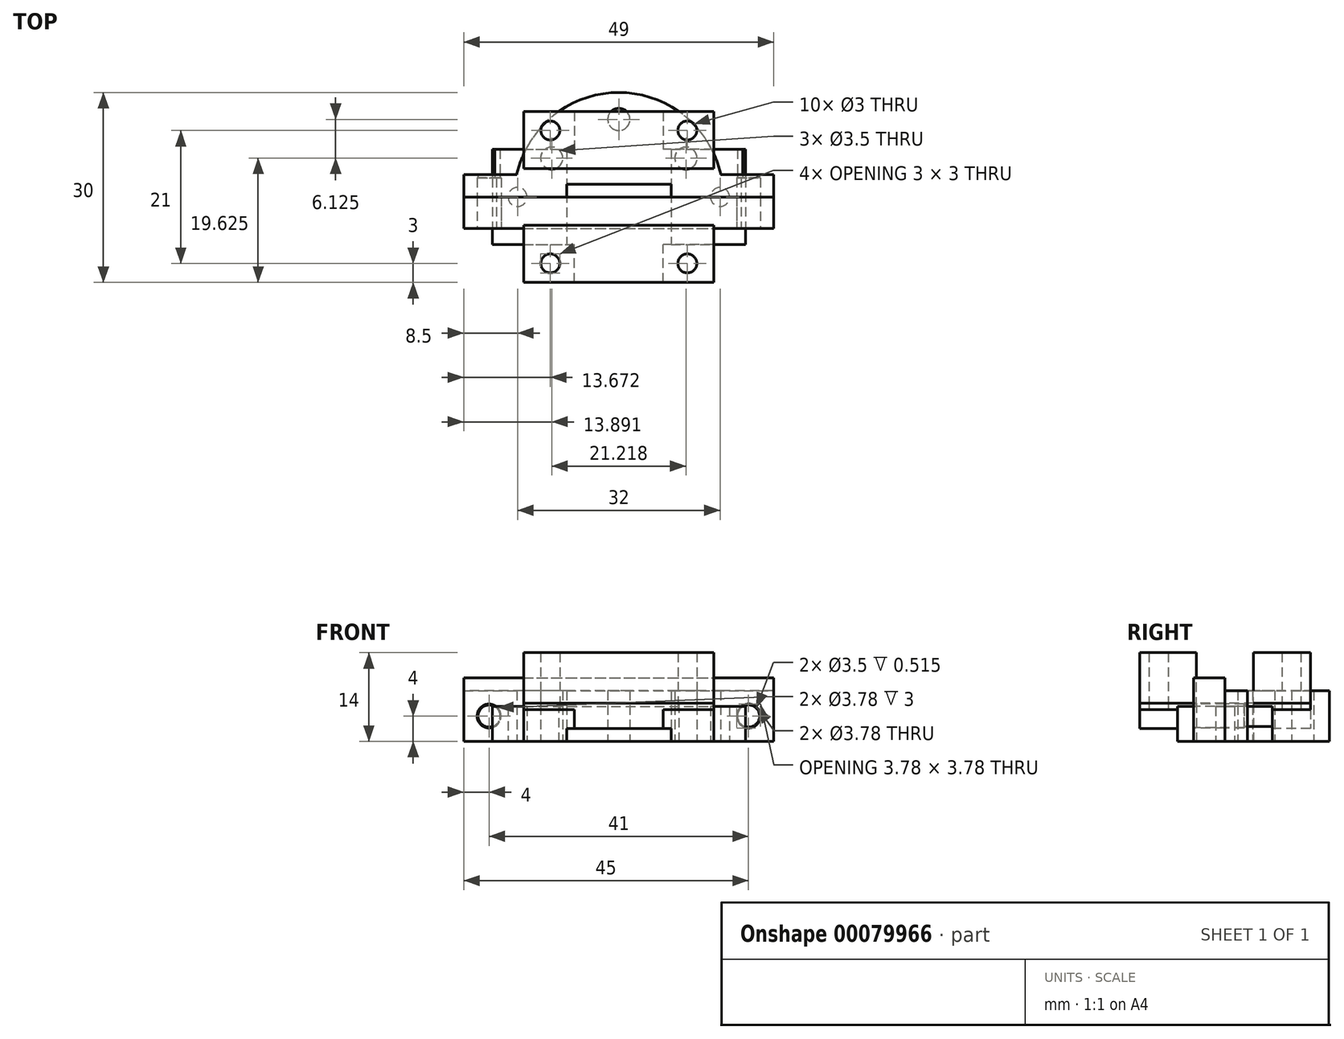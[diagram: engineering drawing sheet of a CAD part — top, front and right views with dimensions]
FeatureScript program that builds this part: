
annotation { "Feature Type Name" : "Feature", "Feature Type Description" : "" }
export const myFeature = defineFeature(function(context is Context, id is Id, definition is map)
    precondition{}
    {
        {
            var Q0;
            Q0=qCreatedBy(makeId("Top.planeOp"),FACE);
            var sketch = newSketch(context, id + "F0", { "sketchPlane" : qUnion([Q0])});
            skLineSegment(sketch, "E0.bottom", {"start": v(-20, 7.5) * mm, "end": v(20, 7.5) * mm});
            skLineSegment(sketch, "E0.top", {"start": v(-20, -7.5) * mm, "end": v(20, -7.5) * mm});
            skLineSegment(sketch, "E0.left", {"start": v(-20, 7.5) * mm, "end": v(-20, -7.5) * mm});
            skLineSegment(sketch, "E0.right", {"start": v(20, 7.5) * mm, "end": v(20, -7.5) * mm});
            skPoint(sketch, "E1", {"position": v(0, 7.5) * mm});
            skPoint(sketch, "E2", {"position": v(20, 0) * mm});
            skLineSegment(sketch, "E3.bottom", {"start": v(-15, 13.5) * mm, "end": v(15, 13.5) * mm});
            skLineSegment(sketch, "E3.top", {"start": v(-15, 7.5) * mm, "end": v(15, 7.5) * mm});
            skLineSegment(sketch, "E3.left", {"start": v(-15, 13.5) * mm, "end": v(-15, 7.5) * mm});
            skLineSegment(sketch, "E3.right", {"start": v(15, 13.5) * mm, "end": v(15, 7.5) * mm});
            skPoint(sketch, "E4", {"position": v(0, 13.5) * mm});
            skLineSegment(sketch, "E5.bottom", {"start": v(-15, -7.5) * mm, "end": v(15, -7.5) * mm});
            skLineSegment(sketch, "E5.top", {"start": v(-15, -13.5) * mm, "end": v(15, -13.5) * mm});
            skLineSegment(sketch, "E5.left", {"start": v(-15, -7.5) * mm, "end": v(-15, -13.5) * mm});
            skLineSegment(sketch, "E5.right", {"start": v(15, -7.5) * mm, "end": v(15, -13.5) * mm});
            skPoint(sketch, "E6", {"position": v(0, -13.5) * mm});
            skCircle(sketch, "E7", {"center": v(-10.83, 10.5) * mm, "radius": 1.5 * mm});
            skPoint(sketch, "E8", {"position": v(-15, 10.5) * mm});
            skCircle(sketch, "E9.MirrorC", {"center": v(10.83, 10.5) * mm, "radius": 1.5 * mm});
            skCircle(sketch, "E10.MirrorC", {"center": v(-10.83, -10.5) * mm, "radius": 1.5 * mm});
            skCircle(sketch, "E11.MirrorC", {"center": v(10.83, -10.5) * mm, "radius": 1.5 * mm});
            skCircle(sketch, "E12", {"center": v(-16, 0) * mm, "radius": 1.5 * mm});
            skCircle(sketch, "E13.MirrorC", {"center": v(16, 0) * mm, "radius": 1.5 * mm});
            skSolve(sketch);
        }
        {
            var Q0;
            Q0 = qSketchRegion(id + "F0", true);
            extrude(context, id + "F1", {"entities" : qUnion([Q0]), "depth" : 14 * mm});
        }
        {
            var Q0;
            Q0=makeQuery(id+"F1.opExtrude","CAP_FACE",FACE,{"disambiguationData":[OSD([sQuery(id+"F0.wireOp",EDGE,"E0.left"),sQuery(id+"F0.wireOp",EDGE,"E0.right"),sQuery(id+"F0.wireOp",EDGE,"E3.bottom"),sQuery(id+"F0.wireOp",EDGE,"E3.top"),sQuery(id+"F0.wireOp",EDGE,"E3.left"),sQuery(id+"F0.wireOp",EDGE,"E3.right"),sQuery(id+"F0.wireOp",EDGE,"E5.bottom"),sQuery(id+"F0.wireOp",EDGE,"E5.top"),sQuery(id+"F0.wireOp",EDGE,"E5.left"),sQuery(id+"F0.wireOp",EDGE,"E5.right")])],"isStart":false});
            var sketch = newSketch(context, id + "F2", { "sketchPlane" : qUnion([Q0])});
            skLineSegment(sketch, "E14.bottom", {"start": v(-15, 4.5) * mm, "end": v(15, 4.5) * mm});
            skLineSegment(sketch, "E14.top", {"start": v(-15, -4.5) * mm, "end": v(15, -4.5) * mm});
            skLineSegment(sketch, "E14.left", {"start": v(-20, 4.5) * mm, "end": v(-20, -4.5) * mm});
            skLineSegment(sketch, "E14.right", {"start": v(20, 4.5) * mm, "end": v(20, -4.5) * mm});
            skPoint(sketch, "E15", {"position": v(0, 4.5) * mm});
            skPoint(sketch, "E16", {"position": v(-20, 0) * mm});
            skPoint(sketch, "E17", {"position": v(20, 0) * mm});
            skLineSegment(sketch, "E18", {"start": v(-15, 7.5) * mm, "end": v(-15, 4.5) * mm});
            skLineSegment(sketch, "E19", {"start": v(-15, 7.5) * mm, "end": v(-20, 7.5) * mm});
            skLineSegment(sketch, "E20", {"start": v(-20, 7.5) * mm, "end": v(-20, 4.5) * mm});
            skLineSegment(sketch, "E21", {"start": v(-20, -4.5) * mm, "end": v(-20, -7.5) * mm});
            skLineSegment(sketch, "E22", {"start": v(-20, -7.5) * mm, "end": v(-15, -7.5) * mm});
            skLineSegment(sketch, "E23", {"start": v(-15, -7.5) * mm, "end": v(-15, -4.5) * mm});
            skLineSegment(sketch, "E24.MirrorCS", {"start": v(15, 7.5) * mm, "end": v(15, 4.5) * mm});
            skLineSegment(sketch, "E25.MirrorCS", {"start": v(15, 7.5) * mm, "end": v(20, 7.5) * mm});
            skLineSegment(sketch, "E26.MirrorCS", {"start": v(20, 7.5) * mm, "end": v(20, 4.5) * mm});
            skLineSegment(sketch, "E27.MirrorCS", {"start": v(20, -4.5) * mm, "end": v(20, -7.5) * mm});
            skLineSegment(sketch, "E28.MirrorCS", {"start": v(20, -7.5) * mm, "end": v(15, -7.5) * mm});
            skLineSegment(sketch, "E29.MirrorCS", {"start": v(15, -7.5) * mm, "end": v(15, -4.5) * mm});
            skSolve(sketch);
        }
        {
            var Q0;
            Q0 = qSketchRegion(id + "F2", true);
            extrude(context, id + "F3", {"entities" : qUnion([Q0]), "operationType" : NewBodyOperationType.REMOVE, "oppositeDirection" : true, "depth" : 8.5 * mm});
        }
        {
            var Q0;
            Q0=qCreatedBy(makeId("Top.planeOp"),FACE);
            var sketch = newSketch(context, id + "F4", { "sketchPlane" : qUnion([Q0])});
            skLineSegment(sketch, "E30.bottom", {"start": v(-15, 13.5) * mm, "end": v(15, 13.5) * mm});
            skLineSegment(sketch, "E30.top", {"start": v(-15, -13.5) * mm, "end": v(15, -13.5) * mm});
            skLineSegment(sketch, "E30.left", {"start": v(-15, 13.5) * mm, "end": v(-15, 4.5) * mm});
            skLineSegment(sketch, "E30.right", {"start": v(15, 13.5) * mm, "end": v(15, 4.5) * mm});
            skCircle(sketch, "E31", {"center": v(-10.83, 10.5) * mm, "radius": 1.5 * mm});
            skCircle(sketch, "E32.MirrorC", {"center": v(10.83, 10.5) * mm, "radius": 1.5 * mm});
            skCircle(sketch, "E33.MirrorC", {"center": v(-10.83, -10.5) * mm, "radius": 1.5 * mm});
            skCircle(sketch, "E34.MirrorC", {"center": v(10.83, -10.5) * mm, "radius": 1.5 * mm});
            skLineSegment(sketch, "E35", {"start": v(-15, 4.5) * mm, "end": v(-9.5, 4.5) * mm});
            skLineSegment(sketch, "E36", {"start": v(-9.5, 4.5) * mm, "end": v(-9.5, -4.5) * mm});
            skLineSegment(sketch, "E37", {"start": v(-9.5, -4.5) * mm, "end": v(-15, -4.5) * mm});
            skPoint(sketch, "E38", {"position": v(-9.5, 0) * mm});
            skLineSegment(sketch, "E39.trimOffspring", {"start": v(-15, -4.5) * mm, "end": v(-15, -13.5) * mm});
            skLineSegment(sketch, "E40.MirrorCS", {"start": v(9.5, 4.5) * mm, "end": v(9.5, -4.5) * mm});
            skLineSegment(sketch, "E41.MirrorCS", {"start": v(15, 4.5) * mm, "end": v(9.5, 4.5) * mm});
            skLineSegment(sketch, "E42.MirrorCS", {"start": v(9.5, -4.5) * mm, "end": v(15, -4.5) * mm});
            skLineSegment(sketch, "E43.trimOffspring", {"start": v(15, -4.5) * mm, "end": v(15, -13.5) * mm});
            skSolve(sketch);
        }
        {
            var Q0;
            Q0 = qSketchRegion(id + "F4", true);
            extrude(context, id + "F5", {"entities" : qUnion([Q0]), "depth" : 6 * mm});
        }
        {
            var Q0;
            Q0=makeQuery(id+"F5.opExtrude","CAP_FACE",FACE,{"disambiguationData":[OSD([sQuery(id+"F4.wireOp",EDGE,"E30.bottom"),sQuery(id+"F4.wireOp",EDGE,"E30.top"),sQuery(id+"F4.wireOp",EDGE,"E30.left"),sQuery(id+"F4.wireOp",EDGE,"E30.right"),sQuery(id+"F4.wireOp",EDGE,"E31"),sQuery(id+"F4.wireOp",EDGE,"E32.MirrorC"),sQuery(id+"F4.wireOp",EDGE,"E33.MirrorC"),sQuery(id+"F4.wireOp",EDGE,"E34.MirrorC")])],"isStart":true});
            var sketch = newSketch(context, id + "F6", { "sketchPlane" : qUnion([Q0])});
            skLineSegment(sketch, "E44.bottom", {"start": v(8.25, -13.5) * mm, "end": v(-8.25, -13.5) * mm});
            skLineSegment(sketch, "E44.top", {"start": v(8.25, 13.5) * mm, "end": v(-8.25, 13.5) * mm});
            skLineSegment(sketch, "E44.left", {"start": v(8.25, -13.5) * mm, "end": v(8.25, 13.5) * mm});
            skLineSegment(sketch, "E44.right", {"start": v(-8.25, -13.5) * mm, "end": v(-8.25, 13.5) * mm});
            skPoint(sketch, "E45", {"position": v(0, -13.5) * mm});
            skPoint(sketch, "E46", {"position": v(0, 0) * mm});
            skSolve(sketch);
        }
        {
            var Q0;
            Q0 = qSketchRegion(id + "F6", true);
            extrude(context, id + "F7", {"entities" : qUnion([Q0]), "operationType" : NewBodyOperationType.REMOVE, "oppositeDirection" : true, "depth" : 2 * mm});
        }
        {
            var Q0;
            Q0=makeQuery(id+"F1.opExtrude","CAP_FACE",FACE,{"disambiguationData":[OSD([sQuery(id+"F0.wireOp",EDGE,"E0.bottom"),sQuery(id+"F0.wireOp",EDGE,"E0.top"),sQuery(id+"F0.wireOp",EDGE,"E0.left"),sQuery(id+"F0.wireOp",EDGE,"E0.right"),sQuery(id+"F0.wireOp",EDGE,"E3.bottom"),sQuery(id+"F0.wireOp",EDGE,"E3.left"),sQuery(id+"F0.wireOp",EDGE,"E3.right"),sQuery(id+"F0.wireOp",EDGE,"E5.top"),sQuery(id+"F0.wireOp",EDGE,"E5.left"),sQuery(id+"F0.wireOp",EDGE,"E5.right"),sQuery(id+"F0.wireOp",EDGE,"E7"),sQuery(id+"F0.wireOp",EDGE,"E9.MirrorC"),sQuery(id+"F0.wireOp",EDGE,"E10.MirrorC"),sQuery(id+"F0.wireOp",EDGE,"E11.MirrorC"),sQuery(id+"F0.wireOp",EDGE,"E12"),sQuery(id+"F0.wireOp",EDGE,"E13.MirrorC")])],"isStart":true});
            var sketch = newSketch(context, id + "F8", { "sketchPlane" : qUnion([Q0])});
            skLineSegment(sketch, "E47.bottom", {"start": v(-15, 13.5) * mm, "end": v(-7, 13.5) * mm});
            skLineSegment(sketch, "E47.top", {"start": v(-15, 7.5) * mm, "end": v(-7, 7.5) * mm});
            skLineSegment(sketch, "E47.left", {"start": v(-15, 13.5) * mm, "end": v(-15, 7.5) * mm});
            skLineSegment(sketch, "E47.right", {"start": v(-7, 13.5) * mm, "end": v(-7, 7.5) * mm});
            skLineSegment(sketch, "E48.MirrorCS", {"start": v(7, 13.5) * mm, "end": v(7, 7.5) * mm});
            skLineSegment(sketch, "E49.MirrorCS", {"start": v(15, 13.5) * mm, "end": v(7, 13.5) * mm});
            skLineSegment(sketch, "E50.MirrorCS", {"start": v(15, 13.5) * mm, "end": v(15, 7.5) * mm});
            skLineSegment(sketch, "E51.MirrorCS", {"start": v(15, 7.5) * mm, "end": v(7, 7.5) * mm});
            skLineSegment(sketch, "E52.MirrorCS", {"start": v(-15, -7.5) * mm, "end": v(-7, -7.5) * mm});
            skLineSegment(sketch, "E53.MirrorCS", {"start": v(-7, -13.5) * mm, "end": v(-7, -7.5) * mm});
            skLineSegment(sketch, "E54.MirrorCS", {"start": v(-15, -13.5) * mm, "end": v(-15, -7.5) * mm});
            skLineSegment(sketch, "E55.MirrorCS", {"start": v(-15, -13.5) * mm, "end": v(-7, -13.5) * mm});
            skLineSegment(sketch, "E56.MirrorCS", {"start": v(15, -7.5) * mm, "end": v(7, -7.5) * mm});
            skLineSegment(sketch, "E57.MirrorCS", {"start": v(7, -13.5) * mm, "end": v(7, -7.5) * mm});
            skLineSegment(sketch, "E58.MirrorCS", {"start": v(15, -13.5) * mm, "end": v(7, -13.5) * mm});
            skLineSegment(sketch, "E59.MirrorCS", {"start": v(15, -13.5) * mm, "end": v(15, -7.5) * mm});
            skSolve(sketch);
        }
        {
            var Q0;
            Q0 = qSketchRegion(id + "F8", true);
            extrude(context, id + "F9", {"entities" : qUnion([Q0]), "operationType" : NewBodyOperationType.REMOVE, "oppositeDirection" : true, "depth" : 5 * mm});
        }
        {
            var Q0;
            Q0=qCreatedBy(makeId("Top.planeOp"),FACE);
            var sketch = newSketch(context, id + "F10", { "sketchPlane" : qUnion([Q0])});
            skLineSegment(sketch, "E60", {"start": v(-16.5, 0) * mm, "end": v(-8.25, 0) * mm});
            skArc(sketch, "E61", {"start": v(16.12, 3.52) * mm, "mid": v(0, 16.5) * mm, "end": v(-16.12, 3.52) * mm});
            skCircle(sketch, "E62", {"center": v(0, 12.25) * mm, "radius": 1.75 * mm});
            skLineSegment(sketch, "E63", {"start": v(-14.29, 8.25) * mm, "end": v(0, 0) * mm, "construction": true});
            skLineSegment(sketch, "E64", {"start": v(0, 0) * mm, "end": v(14.29, 8.25) * mm, "construction": true});
            skCircle(sketch, "E65", {"center": v(-10.6, 6.12) * mm, "radius": 1.75 * mm});
            skCircle(sketch, "E66", {"center": v(10.6, 6.13) * mm, "radius": 1.75 * mm});
            skArc(sketch, "E67", {"start": v(12.25, 0) * mm, "mid": v(0, 12.25) * mm, "end": v(-12.25, 0) * mm, "construction": true});
            skLineSegment(sketch, "E68", {"start": v(-8.25, 0) * mm, "end": v(-8.25, 2) * mm});
            skLineSegment(sketch, "E69", {"start": v(-8.25, 2) * mm, "end": v(8.25, 2) * mm});
            skLineSegment(sketch, "E70", {"start": v(8.25, 2) * mm, "end": v(8.25, 0) * mm});
            skPoint(sketch, "E71", {"position": v(0, 2) * mm});
            skLineSegment(sketch, "E72.trimOffspring", {"start": v(8.25, 0) * mm, "end": v(16.5, 0) * mm});
            skLineSegment(sketch, "E73", {"start": v(-16.5, 0) * mm, "end": v(-24.5, 0) * mm});
            skLineSegment(sketch, "E74", {"start": v(-24.5, 0) * mm, "end": v(-24.5, 3.52) * mm});
            skLineSegment(sketch, "E75", {"start": v(-24.5, 3.52) * mm, "end": v(-16.12, 3.52) * mm});
            skLineSegment(sketch, "E76.MirrorCS", {"start": v(24.5, 3.52) * mm, "end": v(16.12, 3.52) * mm});
            skLineSegment(sketch, "E77.MirrorCS", {"start": v(24.5, 0) * mm, "end": v(24.5, 3.52) * mm});
            skLineSegment(sketch, "E78.MirrorCS", {"start": v(16.5, 0) * mm, "end": v(24.5, 0) * mm});
            skSolve(sketch);
        }
        {
            var Q0;
            Q0 = qSketchRegion(id + "F10", true);
            extrude(context, id + "F11", {"entities" : qUnion([Q0]), "depth" : 8 * mm});
        }
        {
            var Q0;
            Q0=makeQuery(id+"F11.opExtrude","SWEPT_FACE",FACE,{"disambiguationData":[OSD([sQuery(id+"F10.wireOp",EDGE,"E60"),sQuery(id+"F10.wireOp",EDGE,"E73")])]});
            var sketch = newSketch(context, id + "F12", { "sketchPlane" : qUnion([Q0])});
            skCircle(sketch, "E79", {"center": v(-20.5, 4) * mm, "radius": 1.75 * mm});
            skPoint(sketch, "E80", {"position": v(-24.5, 4) * mm});
            skCircle(sketch, "E81.MirrorC", {"center": v(20.5, 4) * mm, "radius": 1.75 * mm});
            skSolve(sketch);
        }
        {
            var Q0;
            Q0 = qSketchRegion(id + "F12", true);
            extrude(context, id + "F13", {"entities" : qUnion([Q0]), "operationType" : NewBodyOperationType.REMOVE, "oppositeDirection" : true, "depth" : 25 * mm});
        }
        {
            var Q0;
            Q0=qCreatedBy(makeId("Top.planeOp"),FACE);
            var sketch = newSketch(context, id + "F14", { "sketchPlane" : qUnion([Q0])});
            skLineSegment(sketch, "E82.bottom", {"start": v(-24.5, 0) * mm, "end": v(24.5, 0) * mm});
            skLineSegment(sketch, "E82.top", {"start": v(-24.5, -5) * mm, "end": v(24.5, -5) * mm});
            skLineSegment(sketch, "E82.left", {"start": v(-24.5, 0) * mm, "end": v(-24.5, -5) * mm});
            skLineSegment(sketch, "E82.right", {"start": v(24.5, 0) * mm, "end": v(24.5, -5) * mm});
            skSolve(sketch);
        }
        {
            var Q0;
            Q0=makeQuery(id+"F14.imprint","IMPRINT",FACE,{"disambiguationData":[TD([[makeQuery(id+"F14.imprint","IMPRINT",EDGE,{"derivedFrom":sQuery(id+"F14.wireOp",EDGE,"E82.bottom")}),-1.0]])]});
            extrude(context, id + "F15", {"entities" : qUnion([Q0]), "depth" : 10 * mm});
        }
        {
            var Q0;
            Q0=makeQuery(id+"F15.opExtrude","SWEPT_FACE",FACE,{"disambiguationData":[OSD([sQuery(id+"F14.wireOp",EDGE,"E82.top")])]});
            var sketch = newSketch(context, id + "F16", { "sketchPlane" : qUnion([Q0])});
            skCircle(sketch, "E83", {"center": v(-20.5, 4) * mm, "radius": 1.89 * mm});
            skCircle(sketch, "E84.MirrorC", {"center": v(20.5, 4) * mm, "radius": 1.89 * mm});
            skSolve(sketch);
        }
        {
            var Q0;
            Q0 = qSketchRegion(id + "F16", true);
            extrude(context, id + "F17", {"entities" : qUnion([Q0]), "operationType" : NewBodyOperationType.REMOVE, "oppositeDirection" : true, "depth" : 8 * mm});
        }
    });
